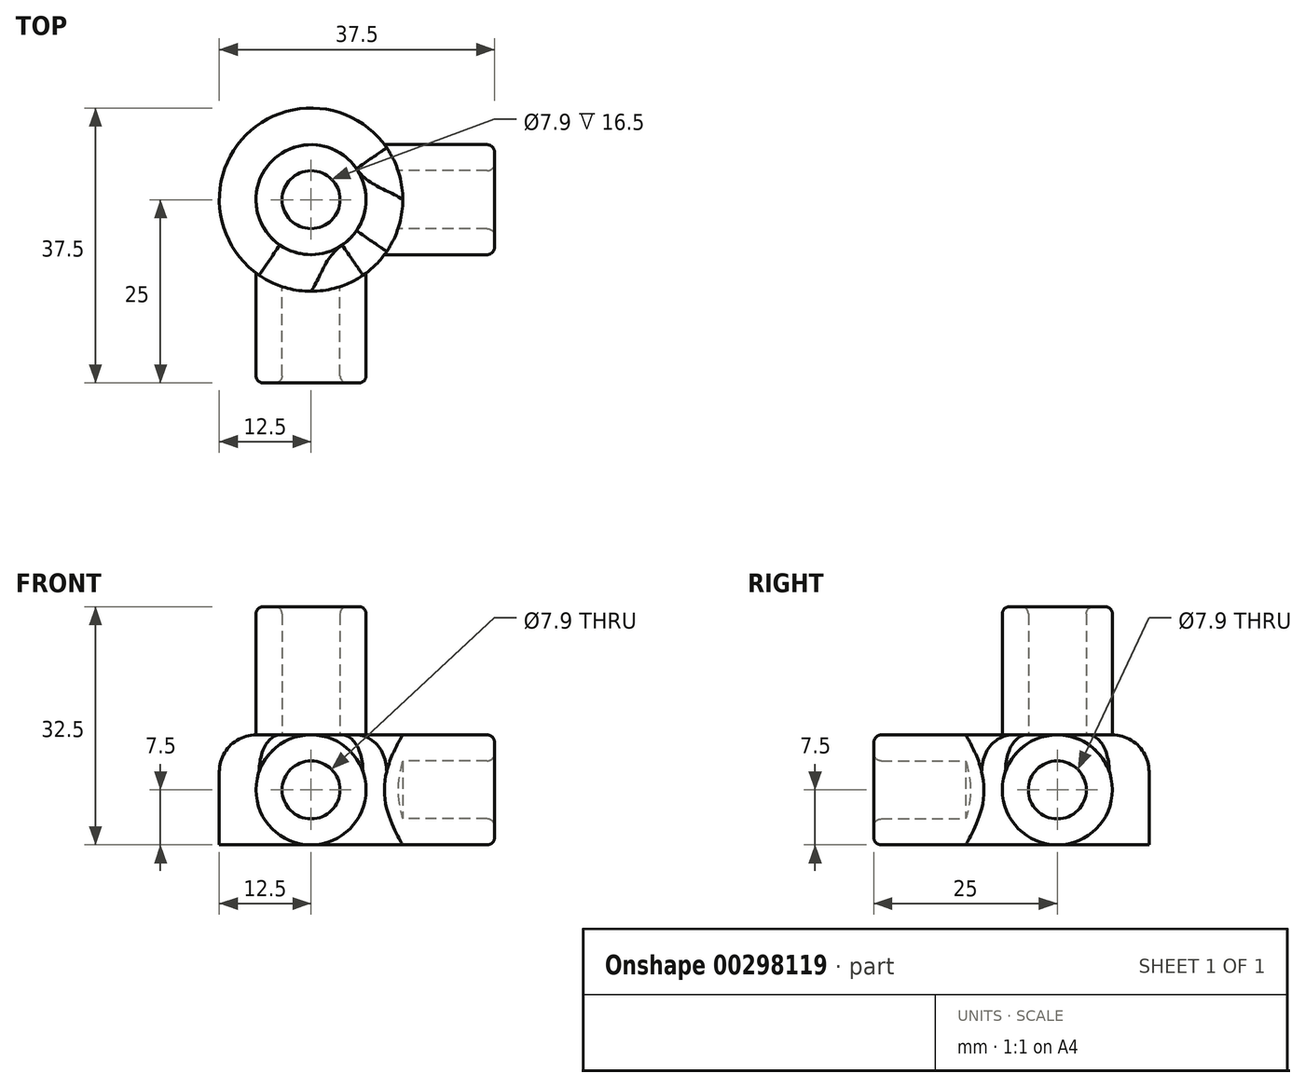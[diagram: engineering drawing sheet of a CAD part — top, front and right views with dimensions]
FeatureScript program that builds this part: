
annotation { "Feature Type Name" : "Feature", "Feature Type Description" : "" }
export const myFeature = defineFeature(function(context is Context, id is Id, definition is map)
    precondition{}
    {
        {
            var Q0;
            Q0=qCreatedBy(makeId("Top.planeOp"),FACE);
            var sketch = newSketch(context, id + "F0", { "sketchPlane" : qUnion([Q0])});
            skCircle(sketch, "E0", {"center": v(0, 0) * mm, "radius": 3.95 * mm});
            skCircle(sketch, "E1", {"center": v(0, 0) * mm, "radius": 7.5 * mm});
            skSolve(sketch);
        }
        {
            var Q0;
            Q0=qCreatedBy(makeId("Right.planeOp"),FACE);
            var sketch = newSketch(context, id + "F1", { "sketchPlane" : qUnion([Q0])});
            skCircle(sketch, "E2", {"center": v(0, 0) * mm, "radius": 3.95 * mm});
            skCircle(sketch, "E3", {"center": v(0, 0) * mm, "radius": 7.5 * mm});
            skSolve(sketch);
        }
        {
            var Q0;
            Q0=qCreatedBy(makeId("Front.planeOp"),FACE);
            var sketch = newSketch(context, id + "F2", { "sketchPlane" : qUnion([Q0])});
            skCircle(sketch, "E4", {"center": v(0, 0) * mm, "radius": 3.95 * mm});
            skCircle(sketch, "E5", {"center": v(0, 0) * mm, "radius": 7.5 * mm});
            skSolve(sketch);
        }
        {
            var Q0;
            Q0=makeQuery(id+"F2.imprint","IMPRINT",FACE,{"disambiguationData":[TD([[makeQuery(id+"F2.imprint","IMPRINT",EDGE,{"derivedFrom":sQuery(id+"F2.wireOp",EDGE,"E4")}),-1.0]])]});
            extrude(context, id + "F3", {"entities" : qUnion([Q0]), "depth" : 25 * mm});
        }
        {
            var Q0;
            Q0=makeQuery(id+"F1.imprint","IMPRINT",FACE,{"disambiguationData":[TD([[makeQuery(id+"F1.imprint","IMPRINT",EDGE,{"derivedFrom":sQuery(id+"F1.wireOp",EDGE,"E2")}),-1.0]])]});
            extrude(context, id + "F4", {"entities" : qUnion([Q0]), "operationType" : NewBodyOperationType.ADD, "depth" : 25 * mm});
        }
        {
            var Q0;
            Q0=makeQuery(id+"F0.imprint","IMPRINT",FACE,{"disambiguationData":[TD([[makeQuery(id+"F0.imprint","IMPRINT",EDGE,{"derivedFrom":sQuery(id+"F0.wireOp",EDGE,"E0")}),-1.0]])]});
            extrude(context, id + "F5", {"entities" : qUnion([Q0]), "operationType" : NewBodyOperationType.ADD, "depth" : 25 * mm});
        }
        {
            var Q0;
            {var subQ0=sQuery(id+"F2.wireOp",EDGE,"E5");var subQ1=makeQuery(id+"F3.opExtrude","SWEPT_FACE",FACE,{"disambiguationData":[OSD([subQ0])]});var subQ2=sQuery(id+"F1.wireOp",EDGE,"E2");var subQ3=makeQuery(id+"F4.opExtrude","SWEPT_FACE",FACE,{"disambiguationData":[OSD([subQ2])]});var subQ4=sQuery(id+"F0.wireOp",EDGE,"E1");var subQ5=sQuery(id+"F2.wireOp",EDGE,"E4");var subQ6=makeQuery(id+"F3.opExtrude","CAP_FACE",FACE,{"disambiguationData":[OSD([subQ5,subQ0])],"isStart":true});var subQ7=sQuery(id+"F0.wireOp",EDGE,"E0");var subQ8=makeQuery(id+"F3.opExtrude","SWEPT_FACE",FACE,{"disambiguationData":[OSD([subQ5])]});var subQ9=sQuery(id+"F1.wireOp",EDGE,"E3");var subQ10=makeQuery(id+"F4.opExtrude","CAP_FACE",FACE,{"disambiguationData":[OSD([subQ2,subQ9])],"isStart":true});var subQ11=makeQuery(id+"F4.opExtrude","SWEPT_FACE",FACE,{"disambiguationData":[OSD([subQ9])]});Q0=makeQuery(id+"F5.boolean.opBoolean","SPLIT",FACE,{"disambiguationData":[TD([subQ8,subQ6,subQ1,subQ3,subQ10,subQ11,makeQuery(id+"F5.opExtrude","SWEPT_FACE",FACE,{"disambiguationData":[OSD([subQ7])]}),makeQuery(id+"F5.opExtrude","CAP_FACE",FACE,{"disambiguationData":[OSD([subQ7,subQ4])],"isStart":true}),makeQuery(id+"F5.opExtrude","SWEPT_FACE",FACE,{"disambiguationData":[OSD([subQ4])]})])],"derivedFrom":makeQuery(id+"F4.boolean.opBoolean","SPLIT",FACE,{"disambiguationData":[TD([subQ8,subQ6,subQ1,subQ3,subQ10,subQ11])],"derivedFrom":subQ6})});}
            var Q1;
            Q1=makeQuery(id+"F4.boolean.opBoolean","INTERSECT",EDGE,{"disambiguationData":[OD(0.0)],"derivedFrom":[makeQuery(id+"F3.opExtrude","CAP_FACE",FACE,{"disambiguationData":[OSD([sQuery(id+"F2.wireOp",EDGE,"E4"),sQuery(id+"F2.wireOp",EDGE,"E5")])],"isStart":true}),makeQuery(id+"F4.opExtrude","CAP_FACE",FACE,{"disambiguationData":[OSD([sQuery(id+"F1.wireOp",EDGE,"E2"),sQuery(id+"F1.wireOp",EDGE,"E3")])],"isStart":true})]});
            revolve(context, id + "F6", {"operationType" : NewBodyOperationType.ADD, "entities" : qUnion([Q0]), "axis" : qUnion([Q1]), "revolveType" : RevolveType.FULL});
        }
        {
            var Q0;
            Q0=makeQuery(id+"F4.opExtrude","CAP_EDGE",EDGE,{"disambiguationData":[OSD([sQuery(id+"F1.wireOp",EDGE,"E2")])],"isStart":false});
            var Q1;
            Q1=makeQuery(id+"F4.opExtrude","CAP_EDGE",EDGE,{"disambiguationData":[OSD([sQuery(id+"F1.wireOp",EDGE,"E3")])],"isStart":false});
            var Q2;
            Q2=makeQuery(id+"F3.opExtrude","CAP_EDGE",EDGE,{"disambiguationData":[OSD([sQuery(id+"F2.wireOp",EDGE,"E4")])],"isStart":false});
            var Q3;
            Q3=makeQuery(id+"F3.opExtrude","CAP_EDGE",EDGE,{"disambiguationData":[OSD([sQuery(id+"F2.wireOp",EDGE,"E5")])],"isStart":false});
            var Q4;
            Q4=makeQuery(id+"F5.opExtrude","CAP_EDGE",EDGE,{"disambiguationData":[OSD([sQuery(id+"F0.wireOp",EDGE,"E0")])],"isStart":false});
            var Q5;
            Q5=makeQuery(id+"F5.opExtrude","CAP_EDGE",EDGE,{"disambiguationData":[OSD([sQuery(id+"F0.wireOp",EDGE,"E1")])],"isStart":false});
            fillet(context, id + "F7", {"entities" : qUnion([Q0, Q1, Q2, Q3, Q4, Q5]), "radius" : 1 * mm, "tangentPropagation" : true, "allowEdgeOverflow" : false});
        }
        {
            var Q0;
            Q0=qCreatedBy(makeId("Top.planeOp"),FACE);
            var sketch = newSketch(context, id + "F8", { "sketchPlane" : qUnion([Q0])});
            skCircle(sketch, "E6", {"center": v(0, 0) * mm, "radius": 12.5 * mm});
            skSolve(sketch);
        }
        {
            var Q0;
            Q0=makeQuery(id+"F8.imprint","IMPRINT",FACE,{"disambiguationData":[TD([[makeQuery(id+"F8.imprint","IMPRINT",EDGE,{"derivedFrom":sQuery(id+"F8.wireOp",EDGE,"E6")}),1.0]])]});
            extrude(context, id + "F9", {"entities" : qUnion([Q0]), "operationType" : NewBodyOperationType.ADD, "endBound" : BoundingType.SYMMETRIC, "depth" : 15 * mm});
        }
        {
            var Q0;
            Q0=makeQuery(id+"F9.boolean.opBoolean","SPLIT",EDGE,{"disambiguationData":[OD(1.0)],"derivedFrom":makeQuery(id+"F9.opExtrude","CAP_EDGE",EDGE,{"disambiguationData":[OSD([sQuery(id+"F8.wireOp",EDGE,"E6")])],"isStart":false})});
            var Q1;
            Q1=makeQuery(id+"F9.boolean.opBoolean","SPLIT",EDGE,{"disambiguationData":[OD(0.0)],"derivedFrom":makeQuery(id+"F9.opExtrude","CAP_EDGE",EDGE,{"disambiguationData":[OSD([sQuery(id+"F8.wireOp",EDGE,"E6")])],"isStart":false})});
            fillet(context, id + "F10", {"entities" : qUnion([Q0, Q1]), "radius" : 5 * mm, "tangentPropagation" : true, "allowEdgeOverflow" : false});
        }
    });
